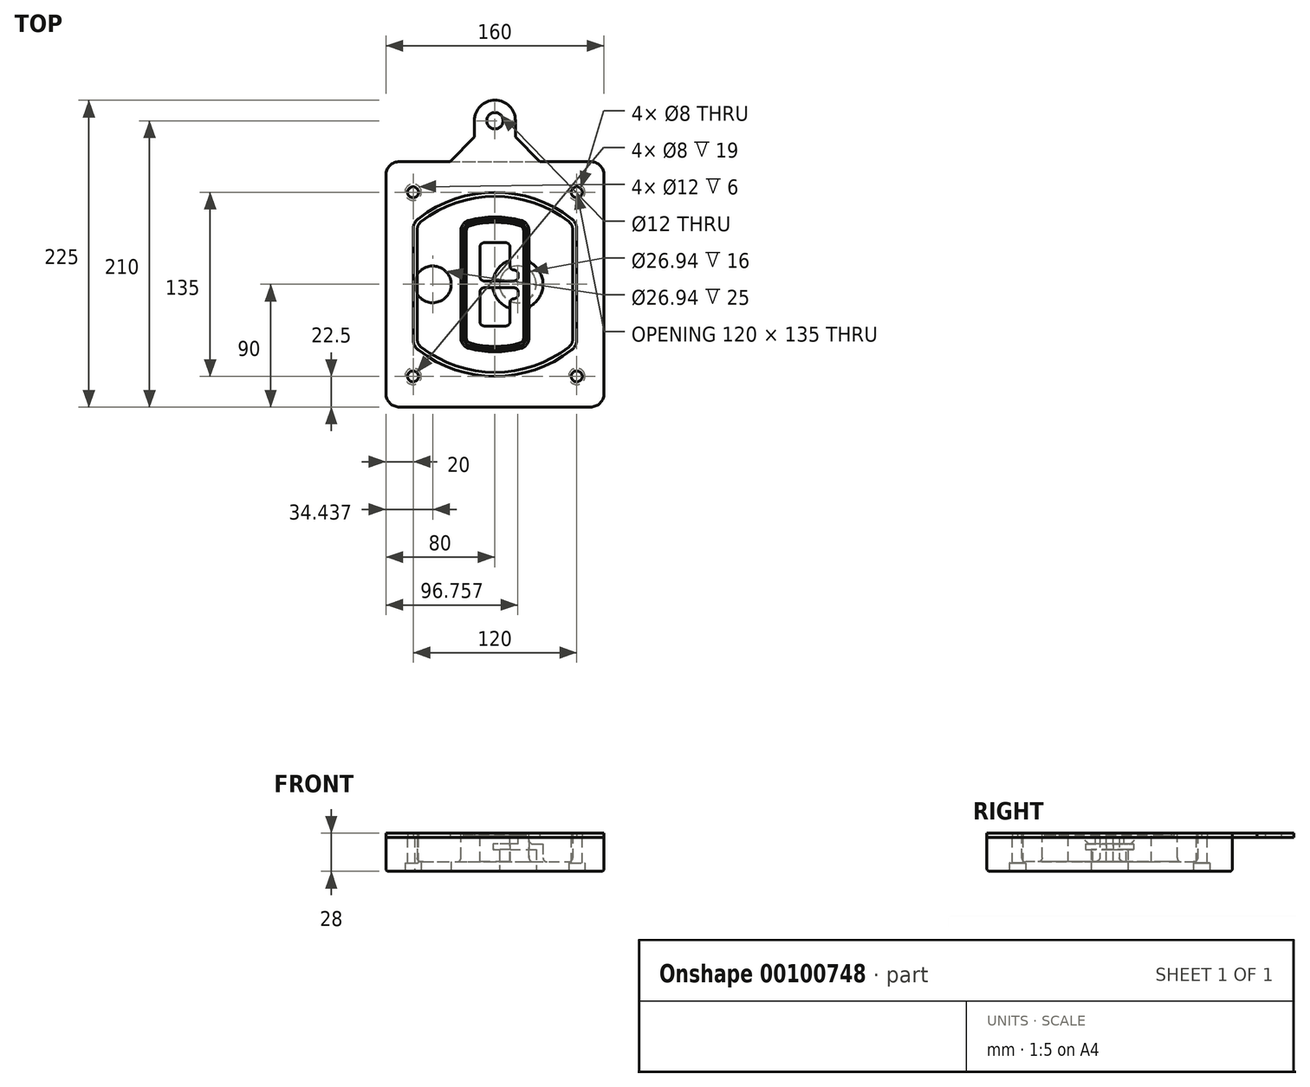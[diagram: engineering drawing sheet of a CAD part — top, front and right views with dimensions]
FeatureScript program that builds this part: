
annotation { "Feature Type Name" : "Feature", "Feature Type Description" : "" }
export const myFeature = defineFeature(function(context is Context, id is Id, definition is map)
    precondition{}
    {
        {
            var Q0;
            Q0=qCreatedBy(makeId("Top.planeOp"),FACE);
            var sketch = newSketch(context, id + "F0", { "sketchPlane" : qUnion([Q0])});
            skPoint(sketch, "E0.rect.middle", {"position": v(0, 0) * mm});
            skLineSegment(sketch, "E1.bottom", {"start": v(-70, -90) * mm, "end": v(70, -90) * mm});
            skLineSegment(sketch, "E1.top", {"start": v(-70, 90) * mm, "end": v(70, 90) * mm});
            skLineSegment(sketch, "E1.left", {"start": v(-80, -80) * mm, "end": v(-80, 80) * mm});
            skLineSegment(sketch, "E1.right", {"start": v(80, -80) * mm, "end": v(80, 80) * mm});
            skLineSegment(sketch, "E2", {"start": v(-80, 90) * mm, "end": v(80, -90) * mm, "construction": true});
            skLineSegment(sketch, "E3", {"start": v(80, 90) * mm, "end": v(-80, -90) * mm, "construction": true});
            skCircle(sketch, "E4", {"center": v(-60, 67.5) * mm, "radius": 4 * mm});
            skCircle(sketch, "E5", {"center": v(60, 67.5) * mm, "radius": 4 * mm});
            skCircle(sketch, "E6", {"center": v(60, -67.5) * mm, "radius": 4 * mm});
            skCircle(sketch, "E7", {"center": v(-60, -67.5) * mm, "radius": 4 * mm});
            skLineSegment(sketch, "E8", {"start": v(-60, 67.5) * mm, "end": v(60, 67.5) * mm, "construction": true});
            skLineSegment(sketch, "E9", {"start": v(60, 67.5) * mm, "end": v(60, -67.5) * mm, "construction": true});
            skLineSegment(sketch, "E10", {"start": v(60, -67.5) * mm, "end": v(-60, -67.5) * mm, "construction": true});
            skLineSegment(sketch, "E11", {"start": v(-60, -67.5) * mm, "end": v(-60, 67.5) * mm, "construction": true});
            skLineSegment(sketch, "E12", {"start": v(-60, 40.3) * mm, "end": v(-60, -40.3) * mm});
            skLineSegment(sketch, "E13", {"start": v(60, 40.3) * mm, "end": v(60, -40.3) * mm});
            skArc(sketch, "E14", {"start": v(56.15, 48.18) * mm, "mid": v(0, 67.5) * mm, "end": v(-56.15, 48.18) * mm});
            skArc(sketch, "E15", {"start": v(-56.15, -48.18) * mm, "mid": v(0, -67.5) * mm, "end": v(56.15, -48.18) * mm});
            skLineSegment(sketch, "E16", {"start": v(-60, 0) * mm, "end": v(60, 0) * mm, "construction": true});
            skPoint(sketch, "E17.visualSharp", {"position": v(-60, -45) * mm});
            skArc(sketch, "E17.filletArc", {"start": v(-60, -40.3) * mm, "mid": v(-58.99, -44.68) * mm, "end": v(-56.15, -48.18) * mm});
            skPoint(sketch, "E18.visualSharp", {"position": v(-60, 45) * mm});
            skArc(sketch, "E18.filletArc", {"start": v(-56.15, 48.18) * mm, "mid": v(-58.99, 44.68) * mm, "end": v(-60, 40.3) * mm});
            skPoint(sketch, "E19.visualSharp", {"position": v(60, 45) * mm});
            skArc(sketch, "E19.filletArc", {"start": v(60, 40.3) * mm, "mid": v(58.99, 44.68) * mm, "end": v(56.15, 48.18) * mm});
            skPoint(sketch, "E20.visualSharp", {"position": v(60, -45) * mm});
            skArc(sketch, "E20.filletArc", {"start": v(56.15, -48.18) * mm, "mid": v(58.99, -44.68) * mm, "end": v(60, -40.3) * mm});
            skPoint(sketch, "E21.visualSharp", {"position": v(-80, 90) * mm});
            skArc(sketch, "E21.filletArc", {"start": v(-70, 90) * mm, "mid": v(-77.07, 87.07) * mm, "end": v(-80, 80) * mm});
            skPoint(sketch, "E22.visualSharp", {"position": v(80, 90) * mm});
            skArc(sketch, "E22.filletArc", {"start": v(80, 80) * mm, "mid": v(77.07, 87.07) * mm, "end": v(70, 90) * mm});
            skPoint(sketch, "E23.visualSharp", {"position": v(80, -90) * mm});
            skArc(sketch, "E23.filletArc", {"start": v(70, -90) * mm, "mid": v(77.07, -87.07) * mm, "end": v(80, -80) * mm});
            skPoint(sketch, "E24.visualSharp", {"position": v(-80, -90) * mm});
            skArc(sketch, "E24.filletArc", {"start": v(-80, -80) * mm, "mid": v(-77.07, -87.07) * mm, "end": v(-70, -90) * mm});
            skArc(sketch, "E25.0", {"start": v(57, 40.3) * mm, "mid": v(56.3, 43.36) * mm, "end": v(54.3, 45.81) * mm});
            skLineSegment(sketch, "E25.1", {"start": v(57, 40.3) * mm, "end": v(57, -40.3) * mm});
            skArc(sketch, "E25.2", {"start": v(54.3, -45.81) * mm, "mid": v(56.3, -43.36) * mm, "end": v(57, -40.3) * mm});
            skArc(sketch, "E25.3", {"start": v(-54.3, -45.81) * mm, "mid": v(0, -64.5) * mm, "end": v(54.3, -45.81) * mm});
            skArc(sketch, "E25.4", {"start": v(-57, -40.3) * mm, "mid": v(-56.3, -43.36) * mm, "end": v(-54.3, -45.81) * mm});
            skArc(sketch, "E25.5", {"start": v(54.3, 45.81) * mm, "mid": v(0, 64.5) * mm, "end": v(-54.3, 45.81) * mm});
            skLineSegment(sketch, "E25.6", {"start": v(-57, 40.3) * mm, "end": v(-57, -40.3) * mm});
            skArc(sketch, "E25.7", {"start": v(-54.3, 45.81) * mm, "mid": v(-56.3, 43.36) * mm, "end": v(-57, 40.3) * mm});
            skArc(sketch, "E26.0", {"start": v(-58.62, 51.33) * mm, "mid": v(-62.58, 46.43) * mm, "end": v(-64, 40.3) * mm});
            skArc(sketch, "E26.1", {"start": v(58.62, 51.33) * mm, "mid": v(0, 71.5) * mm, "end": v(-58.62, 51.33) * mm});
            skArc(sketch, "E26.2", {"start": v(64, 40.3) * mm, "mid": v(62.58, 46.43) * mm, "end": v(58.62, 51.33) * mm});
            skLineSegment(sketch, "E26.3", {"start": v(64, 40.3) * mm, "end": v(64, -40.3) * mm});
            skArc(sketch, "E26.4", {"start": v(58.62, -51.33) * mm, "mid": v(62.58, -46.43) * mm, "end": v(64, -40.3) * mm});
            skLineSegment(sketch, "E26.5", {"start": v(-64, 40.3) * mm, "end": v(-64, -40.3) * mm});
            skArc(sketch, "E26.6", {"start": v(-58.62, -51.33) * mm, "mid": v(0, -71.5) * mm, "end": v(58.62, -51.33) * mm});
            skArc(sketch, "E26.7", {"start": v(-64, -40.3) * mm, "mid": v(-62.58, -46.43) * mm, "end": v(-58.62, -51.33) * mm});
            skSolve(sketch);
        }
        {
            var Q0;
            Q0=makeQuery(id+"F0.imprint","IMPRINT",FACE,{"disambiguationData":[TD([[makeQuery(id+"F0.imprint","IMPRINT",EDGE,{"derivedFrom":sQuery(id+"F0.wireOp",EDGE,"E1.bottom")}),1.0]])]});
            var Q1;
            Q1=makeQuery(id+"F0.imprint","IMPRINT",FACE,{"disambiguationData":[TD([[makeQuery(id+"F0.imprint","IMPRINT",EDGE,{"derivedFrom":sQuery(id+"F0.wireOp",EDGE,"E12")}),1.0]])]});
            var Q2;
            Q2=makeQuery(id+"F0.imprint","IMPRINT",FACE,{"disambiguationData":[TD([[makeQuery(id+"F0.imprint","IMPRINT",EDGE,{"derivedFrom":sQuery(id+"F0.wireOp",EDGE,"E25.0")}),1.0]])]});
            var Q3;
            Q3=makeQuery(id+"F0.imprint","IMPRINT",FACE,{"disambiguationData":[TD([[makeQuery(id+"F0.imprint","IMPRINT",EDGE,{"derivedFrom":sQuery(id+"F0.wireOp",EDGE,"E12")}),-1.0]])]});
            extrude(context, id + "F1", {"entities" : qUnion([Q0, Q1, Q2, Q3]), "oppositeDirection" : true, "depth" : 25 * mm});
        }
        {
            var Q0;
            Q0=makeQuery(id+"F0.imprint","IMPRINT",FACE,{"disambiguationData":[TD([[makeQuery(id+"F0.imprint","IMPRINT",EDGE,{"derivedFrom":sQuery(id+"F0.wireOp",EDGE,"E12")}),1.0]])]});
            extrude(context, id + "F2", {"entities" : qUnion([Q0]), "operationType" : NewBodyOperationType.ADD, "depth" : 3 * mm});
        }
        {
            var Q0;
            Q0=makeQuery(id+"F0.imprint","IMPRINT",FACE,{"disambiguationData":[TD([[makeQuery(id+"F0.imprint","IMPRINT",EDGE,{"derivedFrom":sQuery(id+"F0.wireOp",EDGE,"E25.0")}),1.0]])]});
            extrude(context, id + "F3", {"entities" : qUnion([Q0]), "operationType" : NewBodyOperationType.REMOVE, "oppositeDirection" : true, "depth" : 18 * mm});
        }
        {
            var Q0;
            Q0=makeQuery(id+"F2.opExtrude","CAP_FACE",FACE,{"disambiguationData":[OSD([sQuery(id+"F0.wireOp",EDGE,"E12"),sQuery(id+"F0.wireOp",EDGE,"E13"),sQuery(id+"F0.wireOp",EDGE,"E14"),sQuery(id+"F0.wireOp",EDGE,"E15"),sQuery(id+"F0.wireOp",EDGE,"E17.filletArc"),sQuery(id+"F0.wireOp",EDGE,"E18.filletArc"),sQuery(id+"F0.wireOp",EDGE,"E19.filletArc"),sQuery(id+"F0.wireOp",EDGE,"E20.filletArc"),sQuery(id+"F0.wireOp",EDGE,"E25.0"),sQuery(id+"F0.wireOp",EDGE,"E25.1"),sQuery(id+"F0.wireOp",EDGE,"E25.2"),sQuery(id+"F0.wireOp",EDGE,"E25.3"),sQuery(id+"F0.wireOp",EDGE,"E25.4"),sQuery(id+"F0.wireOp",EDGE,"E25.5"),sQuery(id+"F0.wireOp",EDGE,"E25.6"),sQuery(id+"F0.wireOp",EDGE,"E25.7")])],"isStart":false});
            var sketch = newSketch(context, id + "F4", { "sketchPlane" : qUnion([Q0])});
            skArc(sketch, "E27.0", {"start": v(-19.08, -46.97) * mm, "mid": v(0, -49.5) * mm, "end": v(19.08, -46.97) * mm});
            skArc(sketch, "E28.0", {"start": v(19.08, 46.97) * mm, "mid": v(0, 49.5) * mm, "end": v(-19.08, 46.97) * mm});
            skLineSegment(sketch, "E29", {"start": v(-25, 39.25) * mm, "end": v(-25, -39.25) * mm});
            skLineSegment(sketch, "E30", {"start": v(25, 39.25) * mm, "end": v(25, -39.25) * mm});
            skLineSegment(sketch, "E31", {"start": v(-25, 45.1) * mm, "end": v(25, 45.1) * mm, "construction": true});
            skLineSegment(sketch, "E32", {"start": v(-25, -45.1) * mm, "end": v(25, -45.1) * mm, "construction": true});
            skPoint(sketch, "E33.visualSharp", {"position": v(-25, 45.1) * mm});
            skArc(sketch, "E33.filletArc", {"start": v(-19.08, 46.97) * mm, "mid": v(-23.35, 44.11) * mm, "end": v(-25, 39.25) * mm});
            skPoint(sketch, "E34.visualSharp", {"position": v(25, 45.1) * mm});
            skArc(sketch, "E34.filletArc", {"start": v(25, 39.25) * mm, "mid": v(23.35, 44.11) * mm, "end": v(19.08, 46.97) * mm});
            skPoint(sketch, "E35.visualSharp", {"position": v(25, -45.1) * mm});
            skArc(sketch, "E35.filletArc", {"start": v(19.08, -46.97) * mm, "mid": v(23.35, -44.11) * mm, "end": v(25, -39.25) * mm});
            skPoint(sketch, "E36.visualSharp", {"position": v(-25, -45.1) * mm});
            skArc(sketch, "E36.filletArc", {"start": v(-25, -39.25) * mm, "mid": v(-23.35, -44.11) * mm, "end": v(-19.08, -46.97) * mm});
            skArc(sketch, "E37.0", {"start": v(54.3, 45.81) * mm, "mid": v(0, 64.5) * mm, "end": v(-54.3, 45.81) * mm});
            skArc(sketch, "E37.1", {"start": v(-54.3, 45.81) * mm, "mid": v(-56.3, 43.36) * mm, "end": v(-57, 40.3) * mm});
            skLineSegment(sketch, "E37.2", {"start": v(-57, 40.3) * mm, "end": v(-57, -40.3) * mm});
            skArc(sketch, "E37.3", {"start": v(-57, -40.3) * mm, "mid": v(-56.3, -43.36) * mm, "end": v(-54.3, -45.81) * mm});
            skArc(sketch, "E37.4", {"start": v(-54.3, -45.81) * mm, "mid": v(0, -64.5) * mm, "end": v(54.3, -45.81) * mm});
            skArc(sketch, "E37.5", {"start": v(54.3, -45.81) * mm, "mid": v(56.3, -43.36) * mm, "end": v(57, -40.3) * mm});
            skLineSegment(sketch, "E37.6", {"start": v(57, 40.3) * mm, "end": v(57, -40.3) * mm});
            skArc(sketch, "E37.7", {"start": v(57, 40.3) * mm, "mid": v(56.3, 43.36) * mm, "end": v(54.3, 45.81) * mm});
            skLineSegment(sketch, "E38.0", {"start": v(23, 39.25) * mm, "end": v(23, -39.25) * mm});
            skArc(sketch, "E38.1", {"start": v(18.56, -45.04) * mm, "mid": v(21.76, -42.9) * mm, "end": v(23, -39.25) * mm});
            skArc(sketch, "E38.2", {"start": v(-18.56, -45.04) * mm, "mid": v(0, -47.5) * mm, "end": v(18.56, -45.04) * mm});
            skArc(sketch, "E38.3", {"start": v(-23, -39.25) * mm, "mid": v(-21.76, -42.9) * mm, "end": v(-18.56, -45.04) * mm});
            skLineSegment(sketch, "E38.4", {"start": v(-23, 39.25) * mm, "end": v(-23, -39.25) * mm});
            skArc(sketch, "E38.5", {"start": v(23, 39.25) * mm, "mid": v(21.76, 42.9) * mm, "end": v(18.56, 45.04) * mm});
            skArc(sketch, "E38.6", {"start": v(-18.56, 45.04) * mm, "mid": v(-21.76, 42.9) * mm, "end": v(-23, 39.25) * mm});
            skArc(sketch, "E38.7", {"start": v(18.56, 45.04) * mm, "mid": v(0, 47.5) * mm, "end": v(-18.56, 45.04) * mm});
            skArc(sketch, "E39.0", {"start": v(21, 39.25) * mm, "mid": v(20.18, 41.68) * mm, "end": v(18.04, 43.1) * mm});
            skLineSegment(sketch, "E39.1", {"start": v(21, 39.25) * mm, "end": v(21, -39.25) * mm});
            skArc(sketch, "E39.2", {"start": v(18.04, -43.1) * mm, "mid": v(20.18, -41.68) * mm, "end": v(21, -39.25) * mm});
            skArc(sketch, "E39.3", {"start": v(-18.04, -43.1) * mm, "mid": v(0, -45.5) * mm, "end": v(18.04, -43.1) * mm});
            skArc(sketch, "E39.4", {"start": v(-21, -39.25) * mm, "mid": v(-20.18, -41.68) * mm, "end": v(-18.04, -43.1) * mm});
            skArc(sketch, "E39.5", {"start": v(18.04, 43.1) * mm, "mid": v(0, 45.5) * mm, "end": v(-18.04, 43.1) * mm});
            skLineSegment(sketch, "E39.6", {"start": v(-21, 39.25) * mm, "end": v(-21, -39.25) * mm});
            skArc(sketch, "E39.7", {"start": v(-18.04, 43.1) * mm, "mid": v(-20.18, 41.68) * mm, "end": v(-21, 39.25) * mm});
            skLineSegment(sketch, "E40", {"start": v(-25, 0) * mm, "end": v(25, 0) * mm, "construction": true});
            skLineSegment(sketch, "E41", {"start": v(-11, 5.5) * mm, "end": v(-11, 27.5) * mm});
            skLineSegment(sketch, "E42", {"start": v(-8, 30.5) * mm, "end": v(8, 30.5) * mm});
            skLineSegment(sketch, "E43", {"start": v(11, 27.5) * mm, "end": v(11, 13.5) * mm});
            skLineSegment(sketch, "E44", {"start": v(14, 10.5) * mm, "end": v(14, 10.5) * mm});
            skLineSegment(sketch, "E45", {"start": v(17, 7.5) * mm, "end": v(17, 5.5) * mm});
            skLineSegment(sketch, "E46", {"start": v(14, 2.5) * mm, "end": v(-8, 2.5) * mm});
            skPoint(sketch, "E47.visualSharp", {"position": v(-11, 30.5) * mm});
            skArc(sketch, "E47.filletArc", {"start": v(-8, 30.5) * mm, "mid": v(-10.12, 29.62) * mm, "end": v(-11, 27.5) * mm});
            skPoint(sketch, "E48.visualSharp", {"position": v(11, 30.5) * mm});
            skArc(sketch, "E48.filletArc", {"start": v(11, 27.5) * mm, "mid": v(10.12, 29.62) * mm, "end": v(8, 30.5) * mm});
            skPoint(sketch, "E49.visualSharp", {"position": v(11, 10.5) * mm});
            skArc(sketch, "E49.filletArc", {"start": v(11, 13.5) * mm, "mid": v(11.88, 11.38) * mm, "end": v(14, 10.5) * mm});
            skPoint(sketch, "E50.visualSharp", {"position": v(17, 10.5) * mm});
            skArc(sketch, "E50.filletArc", {"start": v(17, 7.5) * mm, "mid": v(16.12, 9.62) * mm, "end": v(14, 10.5) * mm});
            skPoint(sketch, "E51.visualSharp", {"position": v(17, 2.5) * mm});
            skArc(sketch, "E51.filletArc", {"start": v(14, 2.5) * mm, "mid": v(16.12, 3.38) * mm, "end": v(17, 5.5) * mm});
            skPoint(sketch, "E52.visualSharp", {"position": v(-11, 2.5) * mm});
            skArc(sketch, "E52.filletArc", {"start": v(-11, 5.5) * mm, "mid": v(-10.12, 3.38) * mm, "end": v(-8, 2.5) * mm});
            skLineSegment(sketch, "E53.0.MirrorCS", {"start": v(14, -2.5) * mm, "end": v(-8, -2.5) * mm});
            skArc(sketch, "E54.0.MirrorCS", {"start": v(-11, -5.5) * mm, "mid": v(-10.12, -3.38) * mm, "end": v(-8, -2.5) * mm});
            skLineSegment(sketch, "E55.0.MirrorCS", {"start": v(-11, -5.5) * mm, "end": v(-11, -27.5) * mm});
            skArc(sketch, "E56.0.MirrorCS", {"start": v(-8, -30.5) * mm, "mid": v(-10.12, -29.62) * mm, "end": v(-11, -27.5) * mm});
            skLineSegment(sketch, "E57.0.MirrorCS", {"start": v(-8, -30.5) * mm, "end": v(8, -30.5) * mm});
            skArc(sketch, "E58.0.MirrorCS", {"start": v(11, -27.5) * mm, "mid": v(10.12, -29.62) * mm, "end": v(8, -30.5) * mm});
            skLineSegment(sketch, "E59.0.MirrorCS", {"start": v(11, -27.5) * mm, "end": v(11, -13.5) * mm});
            skArc(sketch, "E60.0.MirrorCS", {"start": v(11, -13.5) * mm, "mid": v(11.88, -11.38) * mm, "end": v(14, -10.5) * mm});
            skArc(sketch, "E61.0.MirrorCS", {"start": v(17, -7.5) * mm, "mid": v(16.12, -9.62) * mm, "end": v(14, -10.5) * mm});
            skLineSegment(sketch, "E62.0.MirrorCS", {"start": v(17, -7.5) * mm, "end": v(17, -5.5) * mm});
            skArc(sketch, "E63.0.MirrorCS", {"start": v(14, -2.5) * mm, "mid": v(16.12, -3.38) * mm, "end": v(17, -5.5) * mm});
            skSolve(sketch);
        }
        {
            var Q0;
            Q0=makeQuery(id+"F4.imprint","IMPRINT",FACE,{"disambiguationData":[TD([[makeQuery(id+"F4.imprint","IMPRINT",EDGE,{"derivedFrom":sQuery(id+"F4.wireOp",EDGE,"E27.0")}),1.0]])]});
            var Q1;
            Q1=makeQuery(id+"F4.imprint","IMPRINT",FACE,{"disambiguationData":[TD([[makeQuery(id+"F4.imprint","IMPRINT",EDGE,{"derivedFrom":sQuery(id+"F4.wireOp",EDGE,"E38.0")}),-1.0]])]});
            var Q2;
            Q2=makeQuery(id+"F4.imprint","IMPRINT",FACE,{"disambiguationData":[TD([[makeQuery(id+"F4.imprint","IMPRINT",EDGE,{"derivedFrom":sQuery(id+"F4.wireOp",EDGE,"E39.0")}),1.0]])]});
            extrude(context, id + "F5", {"entities" : qUnion([Q0, Q1, Q2]), "operationType" : NewBodyOperationType.ADD, "endBound" : BoundingType.UP_TO_NEXT, "oppositeDirection" : true, "depth" : 25 * mm});
        }
        {
            var Q0;
            Q0=makeQuery(id+"F4.imprint","IMPRINT",FACE,{"disambiguationData":[TD([[makeQuery(id+"F4.imprint","IMPRINT",EDGE,{"derivedFrom":sQuery(id+"F4.wireOp",EDGE,"E38.0")}),-1.0]])]});
            extrude(context, id + "F6", {"entities" : qUnion([Q0]), "operationType" : NewBodyOperationType.REMOVE, "oppositeDirection" : true, "depth" : 2 * mm});
        }
        {
            var Q0;
            Q0=makeQuery(id+"F1.opExtrude","CAP_FACE",FACE,{"disambiguationData":[OSD([sQuery(id+"F0.wireOp",EDGE,"E1.bottom"),sQuery(id+"F0.wireOp",EDGE,"E1.top"),sQuery(id+"F0.wireOp",EDGE,"E1.left"),sQuery(id+"F0.wireOp",EDGE,"E1.right"),sQuery(id+"F0.wireOp",EDGE,"E4"),sQuery(id+"F0.wireOp",EDGE,"E5"),sQuery(id+"F0.wireOp",EDGE,"E6"),sQuery(id+"F0.wireOp",EDGE,"E7"),sQuery(id+"F0.wireOp",EDGE,"E21.filletArc"),sQuery(id+"F0.wireOp",EDGE,"E22.filletArc"),sQuery(id+"F0.wireOp",EDGE,"E23.filletArc"),sQuery(id+"F0.wireOp",EDGE,"E24.filletArc")])],"isStart":false});
            var sketch = newSketch(context, id + "F7", { "sketchPlane" : qUnion([Q0])});
            skCircle(sketch, "E64", {"center": v(16.76, 0) * mm, "radius": 13.47 * mm});
            skCircle(sketch, "E65", {"center": v(-45.56, 0) * mm, "radius": 13.47 * mm});
            skLineSegment(sketch, "E66", {"start": v(80, 0) * mm, "end": v(-80, 0) * mm});
            skCircle(sketch, "E67", {"center": v(16.76, 0) * mm, "radius": 18.47 * mm});
            skCircle(sketch, "E68", {"center": v(60, -67.5) * mm, "radius": 6 * mm});
            skCircle(sketch, "E69", {"center": v(-60, -67.5) * mm, "radius": 6 * mm});
            skCircle(sketch, "E70", {"center": v(-60, 67.5) * mm, "radius": 6 * mm});
            skCircle(sketch, "E71", {"center": v(60, 67.5) * mm, "radius": 6 * mm});
            skSolve(sketch);
        }
        {
            var Q0;
            {var subQ1=sQuery(id+"F7.wireOp",EDGE,"E66");var subQ4=sQuery(id+"F7.wireOp",EDGE,"E64");var subQ6=makeQuery(id+"F7.imprint","INTERSECT",VERTEX,{"disambiguationData":[OD(0.0)],"derivedFrom":[subQ4,subQ1]});Q0=makeQuery(id+"F7.imprint","IMPRINT",FACE,{"disambiguationData":[TD([[makeQuery(id+"F7.imprint","IMPRINT",EDGE,{"disambiguationData":[TD([[subQ6,-1.0]])],"derivedFrom":subQ4}),-1.0]])]});}
            var Q1;
            {var subQ0=sQuery(id+"F7.wireOp",EDGE,"E66");var subQ1=sQuery(id+"F7.wireOp",EDGE,"E64");var subQ3=makeQuery(id+"F7.imprint","INTERSECT",VERTEX,{"disambiguationData":[OD(0.0)],"derivedFrom":[subQ1,subQ0]});Q1=makeQuery(id+"F7.imprint","IMPRINT",FACE,{"disambiguationData":[TD([[makeQuery(id+"F7.imprint","IMPRINT",EDGE,{"disambiguationData":[TD([[subQ3,-1.0]])],"derivedFrom":subQ1}),1.0]])]});}
            var Q2;
            {var subQ0=sQuery(id+"F7.wireOp",EDGE,"E66");var subQ1=sQuery(id+"F7.wireOp",EDGE,"E64");var subQ3=makeQuery(id+"F7.imprint","INTERSECT",VERTEX,{"disambiguationData":[OD(0.0)],"derivedFrom":[subQ1,subQ0]});Q2=makeQuery(id+"F7.imprint","IMPRINT",FACE,{"disambiguationData":[TD([[makeQuery(id+"F7.imprint","IMPRINT",EDGE,{"disambiguationData":[TD([[subQ3,1.0]])],"derivedFrom":subQ1}),1.0]])]});}
            var Q3;
            {var subQ1=sQuery(id+"F7.wireOp",EDGE,"E66");var subQ4=sQuery(id+"F7.wireOp",EDGE,"E64");var subQ6=makeQuery(id+"F7.imprint","INTERSECT",VERTEX,{"disambiguationData":[OD(0.0)],"derivedFrom":[subQ4,subQ1]});Q3=makeQuery(id+"F7.imprint","IMPRINT",FACE,{"disambiguationData":[TD([[makeQuery(id+"F7.imprint","IMPRINT",EDGE,{"disambiguationData":[TD([[subQ6,1.0]])],"derivedFrom":subQ4}),-1.0]])]});}
            extrude(context, id + "F8", {"entities" : qUnion([Q0, Q1, Q2, Q3]), "operationType" : NewBodyOperationType.ADD, "oppositeDirection" : true, "depth" : 20 * mm});
        }
        {
            var Q0;
            {var subQ0=sQuery(id+"F7.wireOp",EDGE,"E66");var subQ1=sQuery(id+"F7.wireOp",EDGE,"E64");var subQ3=makeQuery(id+"F7.imprint","INTERSECT",VERTEX,{"disambiguationData":[OD(0.0)],"derivedFrom":[subQ1,subQ0]});Q0=makeQuery(id+"F7.imprint","IMPRINT",FACE,{"disambiguationData":[TD([[makeQuery(id+"F7.imprint","IMPRINT",EDGE,{"disambiguationData":[TD([[subQ3,-1.0]])],"derivedFrom":subQ1}),1.0]])]});}
            var Q1;
            {var subQ0=sQuery(id+"F7.wireOp",EDGE,"E66");var subQ1=sQuery(id+"F7.wireOp",EDGE,"E64");var subQ3=makeQuery(id+"F7.imprint","INTERSECT",VERTEX,{"disambiguationData":[OD(0.0)],"derivedFrom":[subQ1,subQ0]});Q1=makeQuery(id+"F7.imprint","IMPRINT",FACE,{"disambiguationData":[TD([[makeQuery(id+"F7.imprint","IMPRINT",EDGE,{"disambiguationData":[TD([[subQ3,1.0]])],"derivedFrom":subQ1}),1.0]])]});}
            extrude(context, id + "F9", {"entities" : qUnion([Q0, Q1]), "operationType" : NewBodyOperationType.REMOVE, "oppositeDirection" : true, "depth" : 16 * mm});
        }
        {
            var Q0;
            {var subQ0=sQuery(id+"F7.wireOp",EDGE,"E66");var subQ1=sQuery(id+"F7.wireOp",EDGE,"E65");var subQ3=makeQuery(id+"F7.imprint","INTERSECT",VERTEX,{"disambiguationData":[OD(0.0)],"derivedFrom":[subQ1,subQ0]});Q0=makeQuery(id+"F7.imprint","IMPRINT",FACE,{"disambiguationData":[TD([[makeQuery(id+"F7.imprint","IMPRINT",EDGE,{"disambiguationData":[TD([[subQ3,-1.0]])],"derivedFrom":subQ1}),1.0]])]});}
            var Q1;
            {var subQ0=sQuery(id+"F7.wireOp",EDGE,"E66");var subQ1=sQuery(id+"F7.wireOp",EDGE,"E65");var subQ3=makeQuery(id+"F7.imprint","INTERSECT",VERTEX,{"disambiguationData":[OD(0.0)],"derivedFrom":[subQ1,subQ0]});Q1=makeQuery(id+"F7.imprint","IMPRINT",FACE,{"disambiguationData":[TD([[makeQuery(id+"F7.imprint","IMPRINT",EDGE,{"disambiguationData":[TD([[subQ3,1.0]])],"derivedFrom":subQ1}),1.0]])]});}
            extrude(context, id + "F10", {"entities" : qUnion([Q0, Q1]), "operationType" : NewBodyOperationType.REMOVE, "oppositeDirection" : true, "depth" : 25 * mm});
        }
        {
            var Q0;
            Q0=makeQuery(id+"F7.imprint","IMPRINT",FACE,{"disambiguationData":[TD([[makeQuery(id+"F7.imprint","IMPRINT",EDGE,{"derivedFrom":sQuery(id+"F7.wireOp",EDGE,"E68")}),1.0]])]});
            var Q1;
            Q1=makeQuery(id+"F7.imprint","IMPRINT",FACE,{"disambiguationData":[TD([[makeQuery(id+"F7.imprint","IMPRINT",EDGE,{"derivedFrom":makeQuery(id+"F1.opExtrude","CAP_EDGE",EDGE,{"disambiguationData":[OSD([sQuery(id+"F0.wireOp",EDGE,"E5")])],"isStart":false})}),-1.0]])]});
            var Q2;
            Q2=makeQuery(id+"F7.imprint","IMPRINT",FACE,{"disambiguationData":[TD([[makeQuery(id+"F7.imprint","IMPRINT",EDGE,{"derivedFrom":sQuery(id+"F7.wireOp",EDGE,"E69")}),1.0]])]});
            var Q3;
            Q3=makeQuery(id+"F7.imprint","IMPRINT",FACE,{"disambiguationData":[TD([[makeQuery(id+"F7.imprint","IMPRINT",EDGE,{"derivedFrom":makeQuery(id+"F1.opExtrude","CAP_EDGE",EDGE,{"disambiguationData":[OSD([sQuery(id+"F0.wireOp",EDGE,"E4")])],"isStart":false})}),-1.0]])]});
            var Q4;
            Q4=makeQuery(id+"F7.imprint","IMPRINT",FACE,{"disambiguationData":[TD([[makeQuery(id+"F7.imprint","IMPRINT",EDGE,{"derivedFrom":sQuery(id+"F7.wireOp",EDGE,"E70")}),1.0]])]});
            var Q5;
            Q5=makeQuery(id+"F7.imprint","IMPRINT",FACE,{"disambiguationData":[TD([[makeQuery(id+"F7.imprint","IMPRINT",EDGE,{"derivedFrom":makeQuery(id+"F1.opExtrude","CAP_EDGE",EDGE,{"disambiguationData":[OSD([sQuery(id+"F0.wireOp",EDGE,"E7")])],"isStart":false})}),-1.0]])]});
            var Q6;
            Q6=makeQuery(id+"F7.imprint","IMPRINT",FACE,{"disambiguationData":[TD([[makeQuery(id+"F7.imprint","IMPRINT",EDGE,{"derivedFrom":sQuery(id+"F7.wireOp",EDGE,"E71")}),1.0]])]});
            var Q7;
            Q7=makeQuery(id+"F7.imprint","IMPRINT",FACE,{"disambiguationData":[TD([[makeQuery(id+"F7.imprint","IMPRINT",EDGE,{"derivedFrom":makeQuery(id+"F1.opExtrude","CAP_EDGE",EDGE,{"disambiguationData":[OSD([sQuery(id+"F0.wireOp",EDGE,"E6")])],"isStart":false})}),-1.0]])]});
            extrude(context, id + "F11", {"entities" : qUnion([Q0, Q1, Q2, Q3, Q4, Q5, Q6, Q7]), "operationType" : NewBodyOperationType.REMOVE, "oppositeDirection" : true, "depth" : 6 * mm});
        }
        {
            var Q0;
            Q0=makeQuery(id+"F9.boolean.opBoolean","COPY",FACE,{"derivedFrom":makeQuery(id+"F9.opExtrude","CAP_FACE",FACE,{"disambiguationData":[OSD([sQuery(id+"F7.wireOp",EDGE,"E64")])],"isStart":false})});
            var sketch = newSketch(context, id + "F12", { "sketchPlane" : qUnion([Q0])});
            skArc(sketch, "E72.0", {"start": v(11, 17.55) * mm, "mid": v(2.57, 11.82) * mm, "end": v(-1.54, 2.5) * mm});
            skArc(sketch, "E72.1", {"start": v(-1.54, -2.5) * mm, "mid": v(2.57, -11.82) * mm, "end": v(11, -17.55) * mm});
            skLineSegment(sketch, "E73", {"start": v(-1.54, -2.5) * mm, "end": v(14, -2.5) * mm});
            skLineSegment(sketch, "E74.0", {"start": v(14, 2.5) * mm, "end": v(-1.54, 2.5) * mm});
            skArc(sketch, "E74.1", {"start": v(14, 2.5) * mm, "mid": v(16.12, 3.38) * mm, "end": v(17, 5.5) * mm});
            skLineSegment(sketch, "E74.2", {"start": v(17, 7.5) * mm, "end": v(17, 5.5) * mm});
            skArc(sketch, "E74.3", {"start": v(17, 7.5) * mm, "mid": v(16.12, 9.62) * mm, "end": v(14, 10.5) * mm});
            skArc(sketch, "E74.4", {"start": v(11, 13.5) * mm, "mid": v(11.88, 11.38) * mm, "end": v(14, 10.5) * mm});
            skLineSegment(sketch, "E74.5", {"start": v(11, 17.55) * mm, "end": v(11, 13.5) * mm});
            skLineSegment(sketch, "E74.7", {"start": v(14, -2.5) * mm, "end": v(-1.54, -2.5) * mm});
            skArc(sketch, "E74.8", {"start": v(14, -2.5) * mm, "mid": v(16.12, -3.38) * mm, "end": v(17, -5.5) * mm});
            skLineSegment(sketch, "E74.9", {"start": v(17, -7.5) * mm, "end": v(17, -5.5) * mm});
            skArc(sketch, "E74.10", {"start": v(17, -7.5) * mm, "mid": v(16.12, -9.62) * mm, "end": v(14, -10.5) * mm});
            skArc(sketch, "E74.11", {"start": v(11, -13.5) * mm, "mid": v(11.88, -11.38) * mm, "end": v(14, -10.5) * mm});
            skLineSegment(sketch, "E74.12", {"start": v(11, -17.55) * mm, "end": v(11, -13.5) * mm});
            skPoint(sketch, "E75.orphan", {"position": v(11, -27.5) * mm});
            skPoint(sketch, "E76.orphan", {"position": v(-8, -2.5) * mm});
            skPoint(sketch, "E77.orphan", {"position": v(-8, 2.5) * mm});
            skPoint(sketch, "E78.orphan", {"position": v(11, 27.5) * mm});
            skSolve(sketch);
        }
        {
            var Q0;
            {var subQ7=sQuery(id+"F12.wireOp",EDGE,"E72.0");var subQ14=sQuery(id+"F12.wireOp",EDGE,"E72.1");var subQ16=sQuery(id+"F12.wireOp",EDGE,"E74.1");var subQ18=sQuery(id+"F12.wireOp",EDGE,"E74.8");Q0=qUnion([makeQuery(id+"F12.imprint","IMPRINT",FACE,{"disambiguationData":[TD([[makeQuery(id+"F12.imprint","IMPRINT",EDGE,{"derivedFrom":subQ7}),1.0]])]}),makeQuery(id+"F12.imprint","IMPRINT",FACE,{"disambiguationData":[TD([[makeQuery(id+"F12.imprint","IMPRINT",EDGE,{"derivedFrom":subQ14}),1.0]])]}),makeQuery(id+"F12.imprint","IMPRINT",FACE,{"disambiguationData":[TD([[makeQuery(id+"F12.imprint","IMPRINT",EDGE,{"derivedFrom":subQ16}),1.0]])]}),makeQuery(id+"F12.imprint","IMPRINT",FACE,{"disambiguationData":[TD([[makeQuery(id+"F12.imprint","IMPRINT",EDGE,{"derivedFrom":subQ18}),-1.0]])]})]);}
            var Q1;
            Q1=makeQuery(id+"F5.boolean.opBoolean","SPLIT",FACE,{"disambiguationData":[TD([makeQuery(id+"F5.opExtrude","SWEPT_FACE",FACE,{"disambiguationData":[OSD([sQuery(id+"F4.wireOp",EDGE,"E41")])]})])],"derivedFrom":makeQuery(id+"F3.boolean.opBoolean","COPY",FACE,{"derivedFrom":makeQuery(id+"F3.opExtrude","CAP_FACE",FACE,{"disambiguationData":[OSD([sQuery(id+"F0.wireOp",EDGE,"E25.0"),sQuery(id+"F0.wireOp",EDGE,"E25.1"),sQuery(id+"F0.wireOp",EDGE,"E25.2"),sQuery(id+"F0.wireOp",EDGE,"E25.3"),sQuery(id+"F0.wireOp",EDGE,"E25.4"),sQuery(id+"F0.wireOp",EDGE,"E25.5"),sQuery(id+"F0.wireOp",EDGE,"E25.6"),sQuery(id+"F0.wireOp",EDGE,"E25.7")])],"isStart":false})})});
            extrude(context, id + "F13", {"entities" : qUnion([Q0]), "operationType" : NewBodyOperationType.REMOVE, "endBound" : BoundingType.UP_TO_SURFACE, "endBoundEntityFace" : qUnion([Q1]), "depth" : 25 * mm});
        }
        {
            var Q0;
            Q0=makeQuery(id+"F3.boolean.opBoolean","COPY",EDGE,{"derivedFrom":makeQuery(id+"F3.opExtrude","CAP_EDGE",EDGE,{"disambiguationData":[OSD([sQuery(id+"F0.wireOp",EDGE,"E25.6")])],"isStart":false})});
            var Q1;
            Q1=makeQuery(id+"F8.boolean.opBoolean","INTERSECT",EDGE,{"derivedFrom":[makeQuery(id+"F5.opExtrude","SWEPT_FACE",FACE,{"disambiguationData":[OSD([sQuery(id+"F4.wireOp",EDGE,"E30")])]}),makeQuery(id+"F8.opExtrude","CAP_FACE",FACE,{"disambiguationData":[OSD([sQuery(id+"F7.wireOp",EDGE,"E67")])],"isStart":false})]});
            var Q2;
            Q2=makeQuery(id+"F8.boolean.opBoolean","INTERSECT",EDGE,{"disambiguationData":[OD(1.0)],"derivedFrom":[makeQuery(id+"F5.opExtrude","SWEPT_FACE",FACE,{"disambiguationData":[OSD([sQuery(id+"F4.wireOp",EDGE,"E30")])]}),makeQuery(id+"F8.opExtrude","SWEPT_FACE",FACE,{"disambiguationData":[OSD([sQuery(id+"F7.wireOp",EDGE,"E67")])]})]});
            var Q3;
            {var subQ0=sQuery(id+"F4.wireOp",EDGE,"E30");Q3=makeQuery(id+"F8.boolean.opBoolean","SPLIT",EDGE,{"disambiguationData":[TD([makeQuery(id+"F5.opExtrude","SWEPT_FACE",FACE,{"disambiguationData":[OSD([sQuery(id+"F4.wireOp",EDGE,"E35.filletArc")])]})])],"derivedFrom":makeQuery(id+"F5.opExtrude","CAP_EDGE",EDGE,{"disambiguationData":[OSD([subQ0])],"isStart":false})});}
            var Q4;
            {var subQ0=sQuery(id+"F0.wireOp",EDGE,"E25.7");var subQ1=sQuery(id+"F0.wireOp",EDGE,"E25.1");var subQ2=sQuery(id+"F0.wireOp",EDGE,"E25.6");var subQ3=sQuery(id+"F0.wireOp",EDGE,"E25.5");var subQ4=sQuery(id+"F0.wireOp",EDGE,"E25.4");var subQ5=sQuery(id+"F0.wireOp",EDGE,"E25.0");var subQ6=sQuery(id+"F0.wireOp",EDGE,"E25.2");var subQ7=sQuery(id+"F0.wireOp",EDGE,"E25.3");Q4=makeQuery(id+"F8.boolean.opBoolean","INTERSECT",EDGE,{"derivedFrom":[makeQuery(id+"F5.boolean.opBoolean","SPLIT",FACE,{"disambiguationData":[TD([makeQuery(id+"F2.opExtrude","SWEPT_FACE",FACE,{"disambiguationData":[OSD([subQ5])]})])],"derivedFrom":makeQuery(id+"F3.boolean.opBoolean","COPY",FACE,{"derivedFrom":makeQuery(id+"F3.opExtrude","CAP_FACE",FACE,{"disambiguationData":[OSD([subQ5,subQ1,subQ6,subQ7,subQ4,subQ3,subQ2,subQ0])],"isStart":false})})}),makeQuery(id+"F8.opExtrude","SWEPT_FACE",FACE,{"disambiguationData":[OSD([sQuery(id+"F7.wireOp",EDGE,"E67")])]})]});}
            var Q5;
            Q5=makeQuery(id+"F8.boolean.opBoolean","INTERSECT",EDGE,{"disambiguationData":[OD(0.0)],"derivedFrom":[makeQuery(id+"F5.opExtrude","SWEPT_FACE",FACE,{"disambiguationData":[OSD([sQuery(id+"F4.wireOp",EDGE,"E30")])]}),makeQuery(id+"F8.opExtrude","SWEPT_FACE",FACE,{"disambiguationData":[OSD([sQuery(id+"F7.wireOp",EDGE,"E67")])]})]});
            fillet(context, id + "F14", {"entities" : qUnion([Q0, Q1, Q2, Q3, Q4, Q5]), "radius" : 3 * mm, "tangentPropagation" : true, "allowEdgeOverflow" : false});
        }
        {
            var Q0;
            Q0=makeQuery(id+"F1.opExtrude","CAP_EDGE",EDGE,{"disambiguationData":[OSD([sQuery(id+"F0.wireOp",EDGE,"E1.bottom")])],"isStart":false});
            fillet(context, id + "F15", {"entities" : qUnion([Q0]), "radius" : 2 * mm, "tangentPropagation" : true, "allowEdgeOverflow" : false});
        }
        {
            var Q0;
            {var subQ0=sQuery(id+"F0.wireOp",EDGE,"E22.filletArc");var subQ1=sQuery(id+"F0.wireOp",EDGE,"E7");var subQ2=sQuery(id+"F0.wireOp",EDGE,"E6");var subQ3=sQuery(id+"F0.wireOp",EDGE,"E5");var subQ4=sQuery(id+"F0.wireOp",EDGE,"E4");var subQ5=sQuery(id+"F0.wireOp",EDGE,"E1.bottom");var subQ6=sQuery(id+"F0.wireOp",EDGE,"E21.filletArc");var subQ7=sQuery(id+"F0.wireOp",EDGE,"E1.top");var subQ8=sQuery(id+"F0.wireOp",EDGE,"E1.left");var subQ9=sQuery(id+"F0.wireOp",EDGE,"E1.right");var subQ10=sQuery(id+"F0.wireOp",EDGE,"E23.filletArc");var subQ11=sQuery(id+"F0.wireOp",EDGE,"E24.filletArc");Q0=makeQuery(id+"F2.boolean.opBoolean","SPLIT",FACE,{"disambiguationData":[TD([makeQuery(id+"F1.opExtrude","SWEPT_FACE",FACE,{"disambiguationData":[OSD([subQ5])]})])],"derivedFrom":makeQuery(id+"F1.opExtrude","CAP_FACE",FACE,{"disambiguationData":[OSD([subQ5,subQ7,subQ8,subQ9,subQ4,subQ3,subQ2,subQ1,subQ6,subQ0,subQ10,subQ11])],"isStart":true})});}
            var sketch = newSketch(context, id + "F16", { "sketchPlane" : qUnion([Q0])});
            skLineSegment(sketch, "E79", {"start": v(-33, 90) * mm, "end": v(-15, 108) * mm});
            skLineSegment(sketch, "E80", {"start": v(-15, 108) * mm, "end": v(-15, 120) * mm});
            skLineSegment(sketch, "E81", {"start": v(33, 90) * mm, "end": v(15, 108) * mm});
            skLineSegment(sketch, "E82", {"start": v(15, 108) * mm, "end": v(15, 120) * mm});
            skLineSegment(sketch, "E83", {"start": v(0, 90) * mm, "end": v(0, 120) * mm, "construction": true});
            skArc(sketch, "E84", {"start": v(15, 120) * mm, "mid": v(0, 135) * mm, "end": v(-15, 120) * mm});
            skCircle(sketch, "E85", {"center": v(0, 120) * mm, "radius": 6 * mm});
            skLineSegment(sketch, "E86", {"start": v(-80, 0) * mm, "end": v(80, 0) * mm, "construction": true});
            skArc(sketch, "E87.MirrorCS", {"start": v(15, -120) * mm, "mid": v(0, -135) * mm, "end": v(-15, -120) * mm});
            skCircle(sketch, "E88.MirrorC", {"center": v(0, -120) * mm, "radius": 6 * mm});
            skLineSegment(sketch, "E89.MirrorCS", {"start": v(15, -108) * mm, "end": v(15, -120) * mm});
            skLineSegment(sketch, "E90.MirrorCS", {"start": v(-15, -108) * mm, "end": v(-15, -120) * mm});
            skLineSegment(sketch, "E91.MirrorCS", {"start": v(0, -90) * mm, "end": v(0, -120) * mm, "construction": true});
            skLineSegment(sketch, "E92.MirrorCS", {"start": v(33, -90) * mm, "end": v(15, -108) * mm});
            skLineSegment(sketch, "E93.MirrorCS", {"start": v(-33, -90) * mm, "end": v(-15, -108) * mm});
            skSolve(sketch);
        }
        {
            var Q0;
            Q0=makeQuery(id+"F16.imprint","IMPRINT",FACE,{"disambiguationData":[TD([[makeQuery(id+"F16.imprint","IMPRINT",EDGE,{"derivedFrom":makeQuery(id+"F1.opExtrude","CAP_EDGE",EDGE,{"disambiguationData":[OSD([sQuery(id+"F0.wireOp",EDGE,"E1.left")])],"isStart":true})}),-1.0]])]});
            var Q1;
            {var subQ1=sQuery(id+"F16.wireOp",EDGE,"E79");Q1=makeQuery(id+"F16.imprint","IMPRINT",FACE,{"disambiguationData":[TD([[makeQuery(id+"F16.imprint","IMPRINT",EDGE,{"derivedFrom":subQ1}),-1.0]])]});}
            var Q2;
            Q2=makeQuery(id+"F16.imprint","IMPRINT",FACE,{"disambiguationData":[TD([[makeQuery(id+"F16.imprint","IMPRINT",EDGE,{"derivedFrom":sQuery(id+"F16.wireOp",EDGE,"E87.MirrorCS")}),-1.0]])]});
            var Q3;
            Q3=makeQuery(id+"F2.opExtrude","CAP_FACE",FACE,{"disambiguationData":[OSD([sQuery(id+"F0.wireOp",EDGE,"E12"),sQuery(id+"F0.wireOp",EDGE,"E13"),sQuery(id+"F0.wireOp",EDGE,"E14"),sQuery(id+"F0.wireOp",EDGE,"E15"),sQuery(id+"F0.wireOp",EDGE,"E17.filletArc"),sQuery(id+"F0.wireOp",EDGE,"E18.filletArc"),sQuery(id+"F0.wireOp",EDGE,"E19.filletArc"),sQuery(id+"F0.wireOp",EDGE,"E20.filletArc"),sQuery(id+"F0.wireOp",EDGE,"E25.0"),sQuery(id+"F0.wireOp",EDGE,"E25.1"),sQuery(id+"F0.wireOp",EDGE,"E25.2"),sQuery(id+"F0.wireOp",EDGE,"E25.3"),sQuery(id+"F0.wireOp",EDGE,"E25.4"),sQuery(id+"F0.wireOp",EDGE,"E25.5"),sQuery(id+"F0.wireOp",EDGE,"E25.6"),sQuery(id+"F0.wireOp",EDGE,"E25.7")])],"isStart":false});
            extrude(context, id + "F17", {"entities" : qUnion([Q0, Q1, Q2]), "endBound" : BoundingType.UP_TO_SURFACE, "endBoundEntityFace" : qUnion([Q3]), "depth" : 25 * mm});
        }
    });
